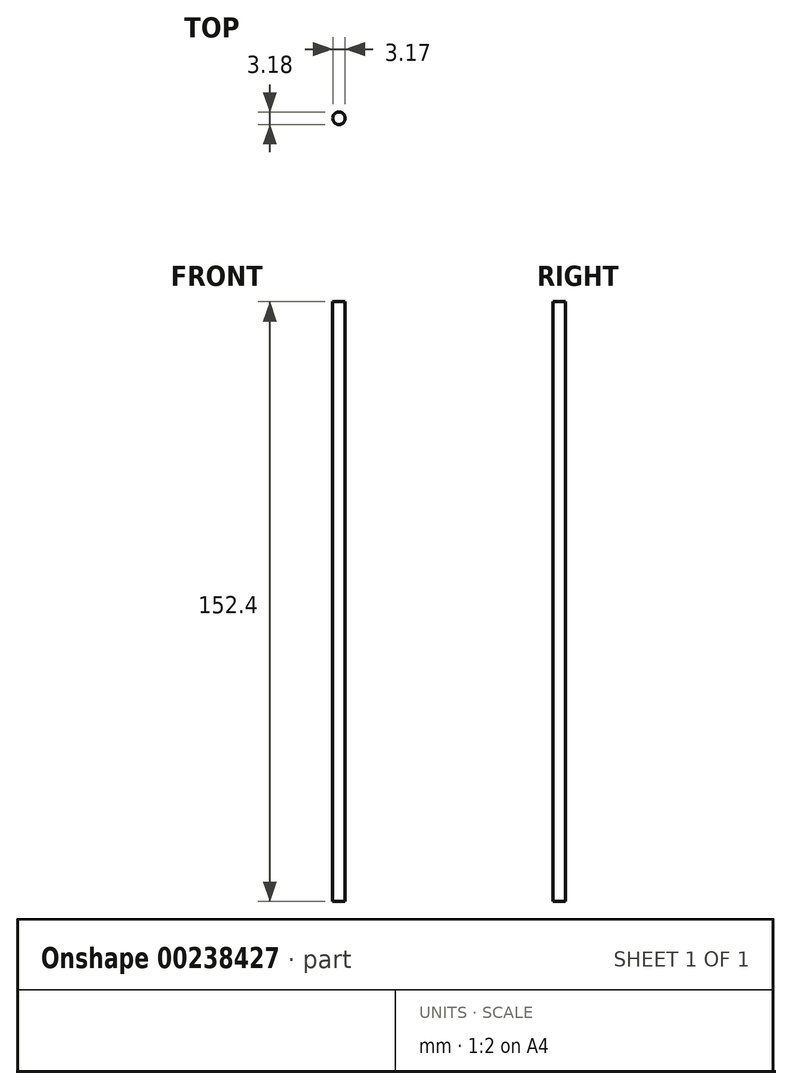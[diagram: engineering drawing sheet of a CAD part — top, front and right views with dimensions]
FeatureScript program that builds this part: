
annotation { "Feature Type Name" : "Feature", "Feature Type Description" : "" }
export const myFeature = defineFeature(function(context is Context, id is Id, definition is map)
    precondition{}
    {
        {
            var Q0;
            Q0=qCreatedBy(makeId("Top.planeOp"),FACE);
            var sketch = newSketch(context, id + "F0", { "sketchPlane" : qUnion([Q0])});
            skCircle(sketch, "E0", {"center": v(-41.44, 8.86) * mm, "radius": 1.59 * mm});
            skSolve(sketch);
        }
        {
            var Q0;
            Q0=makeQuery(id+"F0.imprint","IMPRINT",FACE,{"disambiguationData":[TD([[makeQuery(id+"F0.imprint","IMPRINT",EDGE,{"derivedFrom":sQuery(id+"F0.wireOp",EDGE,"E0")}),1.0]])]});
            extrude(context, id + "F1", {"entities" : qUnion([Q0]), "depth" : 152.4 * mm});
        }
    });
